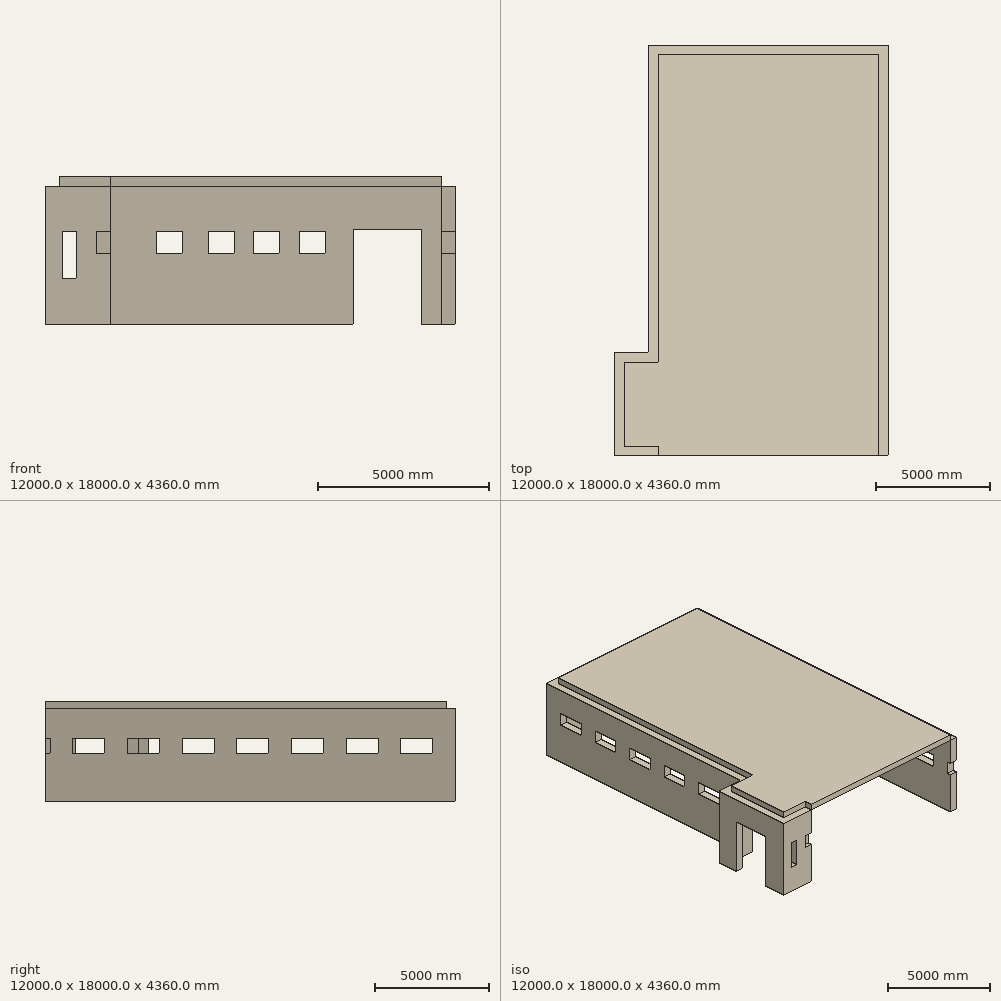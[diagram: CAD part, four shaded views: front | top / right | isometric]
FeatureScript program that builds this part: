
annotation { "Feature Type Name" : "Feature", "Feature Type Description" : "" }
export const myFeature = defineFeature(function(context is Context, id is Id, definition is map)
    precondition{}
    {
        {
            var Q0;
            Q0=qCreatedBy(makeId("Top.planeOp"),FACE);
            var sketch = newSketch(context, id + "F0", { "sketchPlane" : qUnion([Q0])});
            skLineSegment(sketch, "E0", {"start": v(0, 0) * mm, "end": v(0, 18000) * mm});
            skLineSegment(sketch, "E1", {"start": v(0, 18000) * mm, "end": v(-10500, 18000) * mm});
            skLineSegment(sketch, "E2", {"start": v(-10500, 18000) * mm, "end": v(-10500, 4500) * mm});
            skLineSegment(sketch, "E3", {"start": v(-10500, 4500) * mm, "end": v(-12000, 4500) * mm});
            skLineSegment(sketch, "E4", {"start": v(-12000, 4500) * mm, "end": v(-12000, 0) * mm});
            skLineSegment(sketch, "E5.0", {"start": v(-11585, 4085) * mm, "end": v(-11585, 415) * mm});
            skLineSegment(sketch, "E5.1", {"start": v(-10085, 4085) * mm, "end": v(-11585, 4085) * mm});
            skLineSegment(sketch, "E5.2", {"start": v(-10085, 17585) * mm, "end": v(-10085, 4085) * mm});
            skLineSegment(sketch, "E5.3", {"start": v(-415, 17585) * mm, "end": v(-10085, 17585) * mm});
            skLineSegment(sketch, "E5.4", {"start": v(-415, 0) * mm, "end": v(-415, 17585) * mm});
            skLineSegment(sketch, "E6", {"start": v(-12000, 0) * mm, "end": v(-10085, 0) * mm});
            skLineSegment(sketch, "E7", {"start": v(-11585, 415) * mm, "end": v(-10085, 415) * mm});
            skLineSegment(sketch, "E8", {"start": v(-10085, 415) * mm, "end": v(-10085, 0) * mm});
            skLineSegment(sketch, "E9", {"start": v(-415, 0) * mm, "end": v(0, 0) * mm});
            skSolve(sketch);
        }
        {
            var Q0;
            Q0=qSketchRegion(id+"F0",true);
            extrude(context, id + "F1", {"entities" : qUnion([Q0]), "depth" : 4060 * mm});
        }
        {
            var Q0;
            Q0=makeQuery(id+"F1.opExtrude","SWEPT_FACE",FACE,{"disambiguationData":[OSD([sQuery(id+"F0.wireOp",EDGE,"E2")])]});
            var sketch = newSketch(context, id + "F2", { "sketchPlane" : qUnion([Q0])});
            skLineSegment(sketch, "E10.rect.bottom", {"start": v(-15600, 2100) * mm, "end": v(-17000, 2100) * mm});
            skLineSegment(sketch, "E10.rect.top", {"start": v(-15600, 2750) * mm, "end": v(-17000, 2750) * mm});
            skLineSegment(sketch, "E10.rect.left", {"start": v(-15600, 2100) * mm, "end": v(-15600, 2750) * mm});
            skLineSegment(sketch, "E10.rect.right", {"start": v(-17000, 2100) * mm, "end": v(-17000, 2750) * mm});
            skPoint(sketch, "E10.rect.middle", {"position": v(-16300, 2425) * mm});
            skLineSegment(sketch, "E11.rect.bottom", {"start": v(-13200, 2100) * mm, "end": v(-14600, 2100) * mm});
            skLineSegment(sketch, "E11.rect.top", {"start": v(-13200, 2750) * mm, "end": v(-14600, 2750) * mm});
            skLineSegment(sketch, "E11.rect.left", {"start": v(-13200, 2100) * mm, "end": v(-13200, 2750) * mm});
            skLineSegment(sketch, "E11.rect.right", {"start": v(-14600, 2100) * mm, "end": v(-14600, 2750) * mm});
            skPoint(sketch, "E11.rect.middle", {"position": v(-13900, 2425) * mm});
            skLineSegment(sketch, "E12.rect.bottom", {"start": v(-10800, 2100) * mm, "end": v(-12200, 2100) * mm});
            skLineSegment(sketch, "E12.rect.top", {"start": v(-10800, 2750) * mm, "end": v(-12200, 2750) * mm});
            skLineSegment(sketch, "E12.rect.left", {"start": v(-10800, 2100) * mm, "end": v(-10800, 2750) * mm});
            skLineSegment(sketch, "E12.rect.right", {"start": v(-12200, 2100) * mm, "end": v(-12200, 2750) * mm});
            skPoint(sketch, "E12.rect.middle", {"position": v(-11500, 2425) * mm});
            skLineSegment(sketch, "E13.rect.bottom", {"start": v(-8400, 2100) * mm, "end": v(-9800, 2100) * mm});
            skLineSegment(sketch, "E13.rect.top", {"start": v(-8400, 2750) * mm, "end": v(-9800, 2750) * mm});
            skLineSegment(sketch, "E13.rect.left", {"start": v(-8400, 2100) * mm, "end": v(-8400, 2750) * mm});
            skLineSegment(sketch, "E13.rect.right", {"start": v(-9800, 2100) * mm, "end": v(-9800, 2750) * mm});
            skPoint(sketch, "E13.rect.middle", {"position": v(-9100, 2425) * mm});
            skLineSegment(sketch, "E14.rect.bottom", {"start": v(-6000, 2100) * mm, "end": v(-7400, 2100) * mm});
            skLineSegment(sketch, "E14.rect.top", {"start": v(-6000, 2750) * mm, "end": v(-7400, 2750) * mm});
            skLineSegment(sketch, "E14.rect.left", {"start": v(-6000, 2100) * mm, "end": v(-6000, 2750) * mm});
            skLineSegment(sketch, "E14.rect.right", {"start": v(-7400, 2100) * mm, "end": v(-7400, 2750) * mm});
            skPoint(sketch, "E14.rect.middle", {"position": v(-6700, 2425) * mm});
            skLineSegment(sketch, "E15.rect.bottom", {"start": v(-3600, 2100) * mm, "end": v(-5000, 2100) * mm});
            skLineSegment(sketch, "E15.rect.top", {"start": v(-3600, 2750) * mm, "end": v(-5000, 2750) * mm});
            skLineSegment(sketch, "E15.rect.left", {"start": v(-3600, 2100) * mm, "end": v(-3600, 2750) * mm});
            skLineSegment(sketch, "E15.rect.right", {"start": v(-5000, 2100) * mm, "end": v(-5000, 2750) * mm});
            skPoint(sketch, "E15.rect.middle", {"position": v(-4300, 2425) * mm});
            skLineSegment(sketch, "E16.rect.bottom", {"start": v(-1200, 2100) * mm, "end": v(-2600, 2100) * mm});
            skLineSegment(sketch, "E16.rect.top", {"start": v(-1200, 2750) * mm, "end": v(-2600, 2750) * mm});
            skLineSegment(sketch, "E16.rect.left", {"start": v(-1200, 2100) * mm, "end": v(-1200, 2750) * mm});
            skLineSegment(sketch, "E16.rect.right", {"start": v(-2600, 2100) * mm, "end": v(-2600, 2750) * mm});
            skPoint(sketch, "E16.rect.middle", {"position": v(-1900, 2425) * mm});
            skLineSegment(sketch, "E17.rect.bottom", {"start": v(1200, 2100) * mm, "end": v(-200, 2100) * mm});
            skLineSegment(sketch, "E17.rect.top", {"start": v(1200, 2750) * mm, "end": v(-200, 2750) * mm});
            skLineSegment(sketch, "E17.rect.left", {"start": v(1200, 2100) * mm, "end": v(1200, 2750) * mm});
            skLineSegment(sketch, "E17.rect.right", {"start": v(-200, 2100) * mm, "end": v(-200, 2750) * mm});
            skPoint(sketch, "E17.rect.middle", {"position": v(500, 2425) * mm});
            skSolve(sketch);
        }
        {
            var Q0;
            Q0=qSketchRegion(id+"F2",true);
            extrude(context, id + "F3", {"entities" : qUnion([Q0]), "operationType" : NewBodyOperationType.REMOVE, "endBound" : BoundingType.THROUGH_ALL, "oppositeDirection" : true, "depth" : 5000 * mm});
        }
        {
            var Q0;
            Q0=makeQuery(id+"F1.opExtrude","SWEPT_FACE",FACE,{"disambiguationData":[OSD([sQuery(id+"F0.wireOp",EDGE,"E6")])]});
            var sketch = newSketch(context, id + "F4", { "sketchPlane" : qUnion([Q0])});
            skLineSegment(sketch, "E18.rect.bottom", {"start": v(-11100, 1350) * mm, "end": v(-11500, 1350) * mm});
            skLineSegment(sketch, "E18.rect.top", {"start": v(-11100, 2750) * mm, "end": v(-11500, 2750) * mm});
            skLineSegment(sketch, "E18.rect.left", {"start": v(-11100, 1350) * mm, "end": v(-11100, 2750) * mm});
            skLineSegment(sketch, "E18.rect.right", {"start": v(-11500, 1350) * mm, "end": v(-11500, 2750) * mm});
            skPoint(sketch, "E18.rect.middle", {"position": v(-11300, 2050) * mm});
            skSolve(sketch);
        }
        {
            var Q0;
            Q0=qSketchRegion(id+"F4",true);
            extrude(context, id + "F5", {"entities" : qUnion([Q0]), "operationType" : NewBodyOperationType.REMOVE, "endBound" : BoundingType.THROUGH_ALL, "oppositeDirection" : true, "depth" : 25 * mm});
        }
        {
            var Q0;
            Q0=makeQuery(id+"F1.opExtrude","SWEPT_FACE",FACE,{"disambiguationData":[OSD([sQuery(id+"F0.wireOp",EDGE,"E1")])]});
            var sketch = newSketch(context, id + "F6", { "sketchPlane" : qUnion([Q0])});
            skLineSegment(sketch, "E19.bottom", {"start": v(8754.62, 2100) * mm, "end": v(7994.62, 2100) * mm});
            skLineSegment(sketch, "E19.top", {"start": v(8754.62, 2750) * mm, "end": v(7994.62, 2750) * mm});
            skLineSegment(sketch, "E19.left", {"start": v(8754.62, 2100) * mm, "end": v(8754.62, 2750) * mm});
            skLineSegment(sketch, "E19.right", {"start": v(7994.62, 2100) * mm, "end": v(7994.62, 2750) * mm});
            skLineSegment(sketch, "E20.bottom", {"start": v(7234.62, 2100) * mm, "end": v(6474.62, 2100) * mm});
            skLineSegment(sketch, "E20.top", {"start": v(7234.62, 2750) * mm, "end": v(6474.62, 2750) * mm});
            skLineSegment(sketch, "E20.left", {"start": v(7234.62, 2100) * mm, "end": v(7234.62, 2750) * mm});
            skLineSegment(sketch, "E20.right", {"start": v(6474.62, 2100) * mm, "end": v(6474.62, 2750) * mm});
            skLineSegment(sketch, "E21.bottom", {"start": v(5916.25, 2100) * mm, "end": v(5156.25, 2100) * mm});
            skLineSegment(sketch, "E21.top", {"start": v(5916.25, 2750) * mm, "end": v(5156.25, 2750) * mm});
            skLineSegment(sketch, "E21.left", {"start": v(5916.25, 2100) * mm, "end": v(5916.25, 2750) * mm});
            skLineSegment(sketch, "E21.right", {"start": v(5156.25, 2100) * mm, "end": v(5156.25, 2750) * mm});
            skLineSegment(sketch, "E22.bottom", {"start": v(4551.35, 2100) * mm, "end": v(3791.35, 2100) * mm});
            skLineSegment(sketch, "E22.top", {"start": v(4551.35, 2750) * mm, "end": v(3791.35, 2750) * mm});
            skLineSegment(sketch, "E22.left", {"start": v(4551.35, 2100) * mm, "end": v(4551.35, 2750) * mm});
            skLineSegment(sketch, "E22.right", {"start": v(3791.35, 2100) * mm, "end": v(3791.35, 2750) * mm});
            skLineSegment(sketch, "E23.bottom", {"start": v(2999.51, 0) * mm, "end": v(999.51, 0) * mm});
            skLineSegment(sketch, "E23.top", {"start": v(2999.51, 2800) * mm, "end": v(999.51, 2800) * mm});
            skLineSegment(sketch, "E23.left", {"start": v(2999.51, 0) * mm, "end": v(2999.51, 2800) * mm});
            skLineSegment(sketch, "E23.right", {"start": v(999.51, 0) * mm, "end": v(999.51, 2800) * mm});
            skSolve(sketch);
        }
        {
            var Q0;
            Q0=makeQuery(id+"F6.imprint","IMPRINT",FACE,{"disambiguationData":[TD([[makeQuery(id+"F6.imprint","IMPRINT",EDGE,{"derivedFrom":sQuery(id+"F6.wireOp",EDGE,"E23.bottom")}),1.0]])]});
            var Q1;
            Q1=makeQuery(id+"F6.imprint","IMPRINT",FACE,{"disambiguationData":[TD([[makeQuery(id+"F6.imprint","IMPRINT",EDGE,{"derivedFrom":sQuery(id+"F6.wireOp",EDGE,"E22.bottom")}),-1.0]])]});
            var Q2;
            Q2=makeQuery(id+"F6.imprint","IMPRINT",FACE,{"disambiguationData":[TD([[makeQuery(id+"F6.imprint","IMPRINT",EDGE,{"derivedFrom":sQuery(id+"F6.wireOp",EDGE,"E21.bottom")}),-1.0]])]});
            var Q3;
            Q3=makeQuery(id+"F6.imprint","IMPRINT",FACE,{"disambiguationData":[TD([[makeQuery(id+"F6.imprint","IMPRINT",EDGE,{"derivedFrom":sQuery(id+"F6.wireOp",EDGE,"E20.bottom")}),-1.0]])]});
            var Q4;
            Q4=makeQuery(id+"F6.imprint","IMPRINT",FACE,{"disambiguationData":[TD([[makeQuery(id+"F6.imprint","IMPRINT",EDGE,{"derivedFrom":sQuery(id+"F6.wireOp",EDGE,"E19.bottom")}),-1.0]])]});
            extrude(context, id + "F7", {"entities" : qUnion([Q0, Q1, Q2, Q3, Q4]), "operationType" : NewBodyOperationType.REMOVE, "endBound" : BoundingType.THROUGH_ALL, "oppositeDirection" : true, "depth" : 25 * mm});
        }
        {
            var Q0;
            Q0=makeQuery(id+"F1.opExtrude","SWEPT_FACE",FACE,{"disambiguationData":[OSD([sQuery(id+"F0.wireOp",EDGE,"E4")])]});
            var sketch = newSketch(context, id + "F8", { "sketchPlane" : qUnion([Q0])});
            skLineSegment(sketch, "E24.bottom", {"start": v(-1300, 0) * mm, "end": v(-3300, 0) * mm});
            skLineSegment(sketch, "E24.top", {"start": v(-1300, 2800) * mm, "end": v(-3300, 2800) * mm});
            skLineSegment(sketch, "E24.left", {"start": v(-1300, 0) * mm, "end": v(-1300, 2800) * mm});
            skLineSegment(sketch, "E24.right", {"start": v(-3300, 0) * mm, "end": v(-3300, 2800) * mm});
            skSolve(sketch);
        }
        {
            var Q0;
            Q0=makeQuery(id+"F8.imprint","IMPRINT",FACE,{"disambiguationData":[TD([[makeQuery(id+"F8.imprint","IMPRINT",EDGE,{"derivedFrom":sQuery(id+"F8.wireOp",EDGE,"E24.bottom")}),1.0]])]});
            extrude(context, id + "F9", {"entities" : qUnion([Q0]), "operationType" : NewBodyOperationType.REMOVE, "oppositeDirection" : true, "depth" : 1000 * mm});
        }
        {
            var Q0;
            Q0=makeQuery(id+"F1.opExtrude","CAP_FACE",FACE,{"disambiguationData":[OSD([sQuery(id+"F0.wireOp",EDGE,"E0"),sQuery(id+"F0.wireOp",EDGE,"E1"),sQuery(id+"F0.wireOp",EDGE,"E2"),sQuery(id+"F0.wireOp",EDGE,"E3"),sQuery(id+"F0.wireOp",EDGE,"E4"),sQuery(id+"F0.wireOp",EDGE,"E5.0"),sQuery(id+"F0.wireOp",EDGE,"E5.1"),sQuery(id+"F0.wireOp",EDGE,"E5.2"),sQuery(id+"F0.wireOp",EDGE,"E5.3"),sQuery(id+"F0.wireOp",EDGE,"E5.4"),sQuery(id+"F0.wireOp",EDGE,"E6"),sQuery(id+"F0.wireOp",EDGE,"E7"),sQuery(id+"F0.wireOp",EDGE,"E8"),sQuery(id+"F0.wireOp",EDGE,"E9")])],"isStart":false});
            var sketch = newSketch(context, id + "F10", { "sketchPlane" : qUnion([Q0])});
            skLineSegment(sketch, "E25.0", {"start": v(-10085, 17585) * mm, "end": v(-10085, 4085) * mm});
            skLineSegment(sketch, "E25.1", {"start": v(-415, 0) * mm, "end": v(-415, 17585) * mm});
            skLineSegment(sketch, "E25.2", {"start": v(-415, 17585) * mm, "end": v(-10085, 17585) * mm});
            skLineSegment(sketch, "E25.3", {"start": v(-10085, 4085) * mm, "end": v(-11585, 4085) * mm});
            skLineSegment(sketch, "E25.4", {"start": v(-11585, 4085) * mm, "end": v(-11585, 415) * mm});
            skLineSegment(sketch, "E25.5", {"start": v(-11585, 415) * mm, "end": v(-10085, 415) * mm});
            skLineSegment(sketch, "E25.6", {"start": v(-10085, 415) * mm, "end": v(-10085, 0) * mm});
            skLineSegment(sketch, "E26", {"start": v(-10085, 0) * mm, "end": v(-415, 0) * mm});
            skSolve(sketch);
        }
        {
            var Q0;
            Q0=makeQuery(id+"F10.imprint","IMPRINT",FACE,{"disambiguationData":[TD([[makeQuery(id+"F10.imprint","IMPRINT",EDGE,{"derivedFrom":sQuery(id+"F10.wireOp",EDGE,"E25.0")}),1.0]])]});
            extrude(context, id + "F11", {"entities" : qUnion([Q0]), "depth" : 300 * mm});
        }
    });
